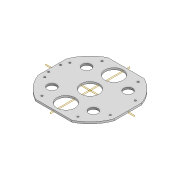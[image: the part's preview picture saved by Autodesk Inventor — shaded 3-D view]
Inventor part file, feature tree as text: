
AUTODESK INVENTOR PART (.ipt)
format: ipt  version: 2022 (Build 260153000, 153)  size: 189,952 bytes
history: native  units: mm
features: extrude x3, plane x2, mirror x2, sketch x2, projected_geometry x1
ambient origin geometry x8: Origin, YZ Plane, XZ Plane, XY Plane, X Axis, Y Axis, Z Axis, Center Point
bodies: Solid1 (feature_tree)
feature tree (10):
  extrude  "Extrusion1"  Depth=3.0mm TaperAngle=0.0deg
  extrude  "Extrusion3"  Depth=10.0mm
  plane  "Work Plane5"
  plane  "Work Plane6"
  mirror  "Mirror3"
  mirror  "Mirror4"
  sketch  "Sketch10"  dims[d0=120.0mm d2=3.0mm d3=0.0mm]
  extrude  "Extrusion6"  Depth=10.0mm TaperAngle=0.0deg
  projected_geometry  "Projected Loop6"
  sketch  "Sketch14"  dims[d25=60.0mm d27=8.726646mm d36=10.0mm d37=0.0mm d38=63.0mm d39=63.0mm d50=3.0mm d51=10.0mm d52=25.0mm d53=40.0mm d54=30.0mm d55=40.0mm d56=15.0mm d57=45.0mm d58=30.0mm d75=3.0mm d76=3.0mm d77=4.0mm d78=4.0mm d79=10.0mm d80=10.0mm d81=10.0mm d82=0.0mm]
